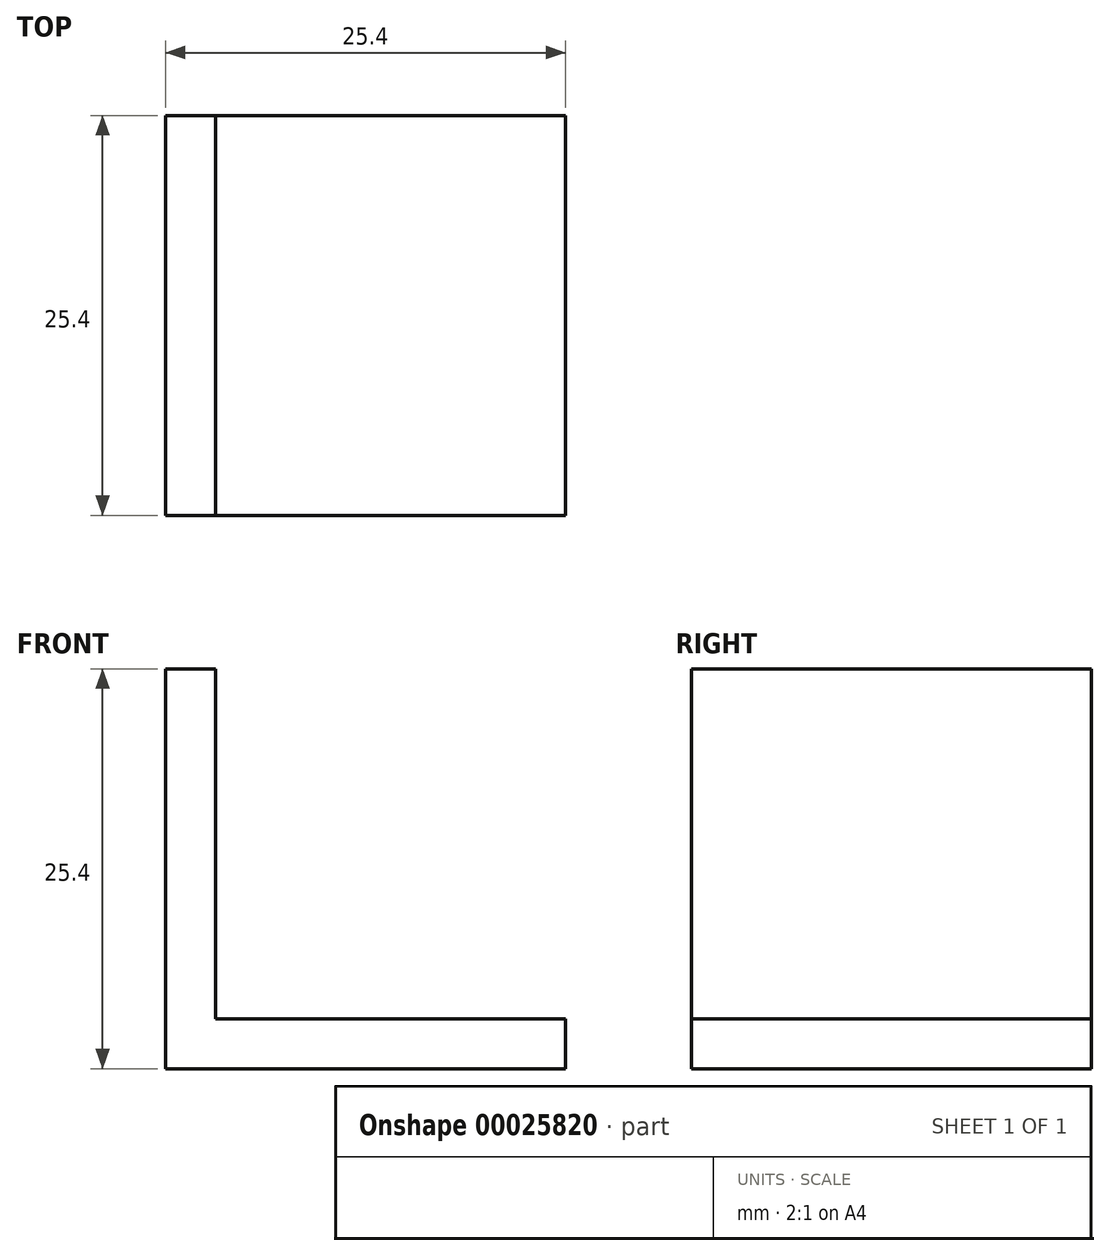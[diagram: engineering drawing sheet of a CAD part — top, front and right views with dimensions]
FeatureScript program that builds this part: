
annotation { "Feature Type Name" : "Feature", "Feature Type Description" : "" }
export const myFeature = defineFeature(function(context is Context, id is Id, definition is map)
    precondition{}
    {
        {
            var Q0;
            Q0=qCreatedBy(makeId("Front.planeOp"),FACE);
            var sketch = newSketch(context, id + "F0", { "sketchPlane" : qUnion([Q0])});
            skLineSegment(sketch, "E0.bottom", {"start": v(0, 0) * mm, "end": v(25.4, 0) * mm});
            skLineSegment(sketch, "E0.top", {"start": v(0, 25.4) * mm, "end": v(3.17, 25.4) * mm});
            skLineSegment(sketch, "E0.left", {"start": v(0, 0) * mm, "end": v(0, 25.4) * mm});
            skLineSegment(sketch, "E0.right", {"start": v(25.4, 0) * mm, "end": v(25.4, 3.18) * mm});
            skLineSegment(sketch, "E1.bottom", {"start": v(3.17, 3.17) * mm, "end": v(25.4, 3.17) * mm});
            skLineSegment(sketch, "E1.left", {"start": v(3.17, 3.18) * mm, "end": v(3.17, 25.4) * mm});
            skSolve(sketch);
        }
        {
            var Q0;
            Q0 = qSketchRegion(id + "F0", true);
            extrude(context, id + "F1", {"entities" : qUnion([Q0]), "endBound" : BoundingType.SYMMETRIC, "depth" : 25.4 * mm});
        }
    });
